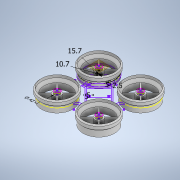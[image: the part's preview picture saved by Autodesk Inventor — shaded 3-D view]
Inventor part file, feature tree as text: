
AUTODESK INVENTOR PART (.ipt)
format: ipt  version: 2021 (Build 250183000, 183)  size: 423,424 bytes
history: native  units: in
note: dims shown in document units (in); Inventor stores cm internally (conversion verified against a paired STEP export)
features: mirror x12, sketch x7, plane x7, extrude x4, chamfer x3, other x2
ambient origin geometry x8: Origin, YZ Plane, XZ Plane, XY Plane, X Axis, Y Axis, Z Axis, Center Point
bodies: Body1 (feature_tree)
feature tree (35):
  other  "Annotations"
  sketch  "Sketch1"  dims[d16=0.5in d17=0.0in d18=0.189in d19=0.0787in d20=30.0deg d27=1.5748in d28=1.5748in]
  extrude  "Extrusion3"  Depth=0.5in TaperAngle=30.0deg
  chamfer  "Chamfer1"  Distance=1.5748in
  sketch  "Sketch3"  dims[d32=0.1969in d49=2.5197in d50=0.3937in d51=0.0in]
  plane  "Work Plane1"
  plane  "Work Plane2"
  mirror  "Mirror1"
  mirror  "Mirror3"
  mirror  "Mirror4"
  plane  "Work Plane6"
  extrude  "Extrusion7"  Depth=0.3937in
  chamfer  "Chamfer5"  Distance=0.3937in
  mirror  "Mirror5"
  mirror  "Mirror6"
  mirror  "Mirror7"
  extrude  "Extrusion12"  Depth=0.4213in
  mirror  "Mirror8"
  mirror  "Mirror9"
  mirror  "Mirror10"
  sketch  "Sketch17"  dims[d52=0.0787in d53=0.0787in d54=45.0deg d82=0.4213in]
  chamfer  "Chamfer9"  Distance=0.311in
  sketch  "Sketch22"  dims[d83=0.6181in d84=0.311in d85=0.0in]
  plane  "Work Plane7"
  sketch  "Sketch23"  dims[d146=0.0866in d147=0.0787in d148=45.0deg d182=0.1457in d183=0.0in]
  plane  "Work Plane8"
  sketch  "Sketch24"  dims[d184=0.1457in d185=0.0in]
  extrude  "Extrusion21"  Depth=0.1457in TaperAngle=0.0deg
  mirror  "Mirror11"
  mirror  "Mirror12"
  mirror  "Mirror13"
  plane  "Work Plane4"
  plane  "Work Plane5"
  sketch  "Sketch26"  dims[d240=0.0394in d241=0.0in d253=0.1969in d254=0.1969in d261=0.1969in d262=0.1969in d285=0.0984in d242=0.592in d243=0.4213in d12=0.0197in d13=0.0344in d14=0.0197in d15=0.0344in d229=0.0197in d230=0.0344in d231=0.0197in d232=0.0344in]
  other  "Diameter Dimension 1"
